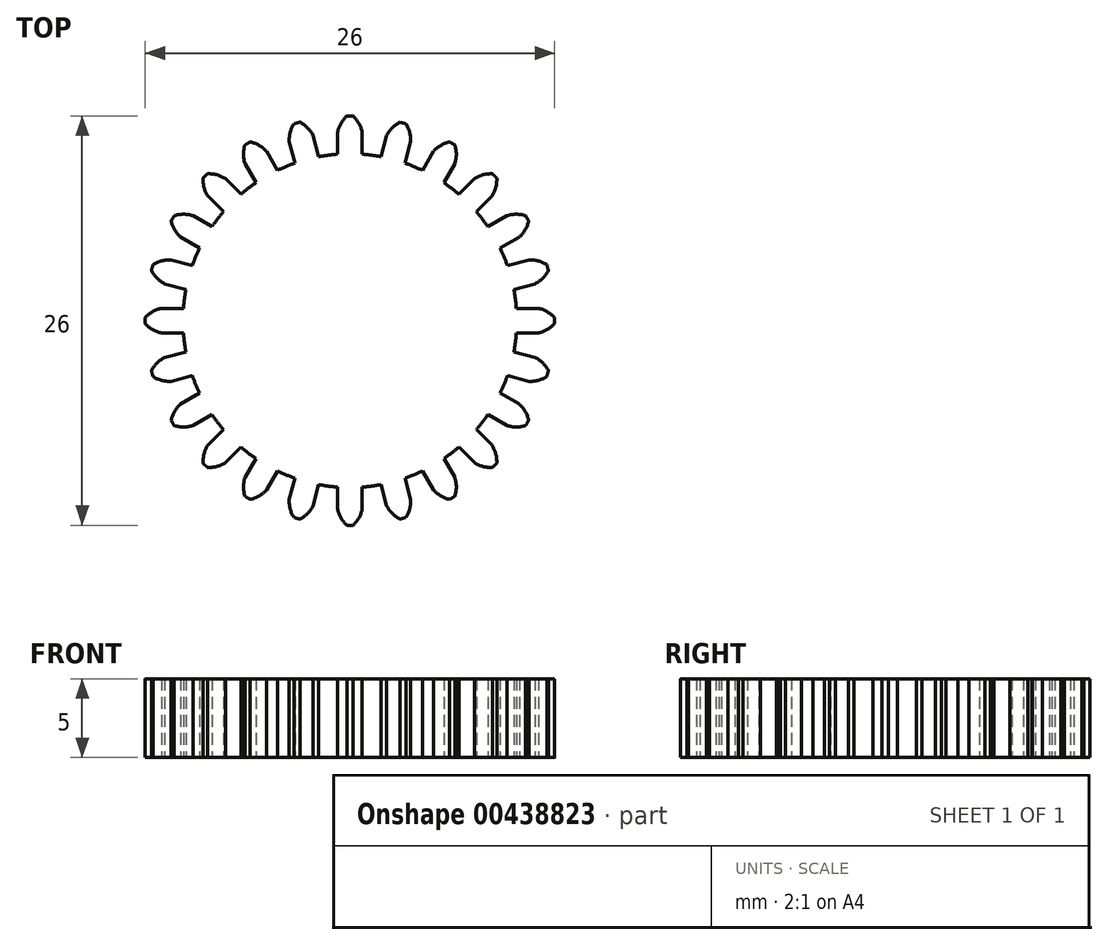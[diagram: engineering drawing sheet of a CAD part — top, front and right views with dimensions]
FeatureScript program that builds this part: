
annotation { "Feature Type Name" : "Feature", "Feature Type Description" : "" }
export const myFeature = defineFeature(function(context is Context, id is Id, definition is map)
    precondition{}
    {
        {
            var Q0;
            Q0=qCreatedBy(makeId("Top.planeOp"),FACE);
            var sketch = newSketch(context, id + "F0", { "sketchPlane" : qUnion([Q0])});
            skArc(sketch, "E0", {"start": v(-0.79, 12.98) * mm, "mid": v(0, -13) * mm, "end": v(0.79, 12.98) * mm, "construction": true});
            skCircle(sketch, "E1", {"center": v(0, 0) * mm, "radius": 12 * mm, "construction": true});
            skCircle(sketch, "E2", {"center": v(0, 0) * mm, "radius": 10.6 * mm, "construction": true});
            skLineSegment(sketch, "E3", {"start": v(-0.79, 10.57) * mm, "end": v(-0.79, 11.97) * mm});
            skLineSegment(sketch, "E4", {"start": v(0.79, 10.57) * mm, "end": v(0.79, 12.98) * mm});
            skArc(sketch, "E5", {"start": v(-0.2, 13) * mm, "mid": v(0, 13) * mm, "end": v(0.2, 13) * mm});
            skPoint(sketch, "E6.center", {"position": v(0.46, 5.44) * mm});
            skArc(sketch, "E7", {"start": v(0.79, 10.57) * mm, "mid": v(2.01, 10.4) * mm, "end": v(3.21, 10.1) * mm});
            skArc(sketch, "E8.1.0", {"start": v(-1.98, 10.41) * mm, "mid": v(-0.75, 10.57) * mm, "end": v(0.5, 10.59) * mm});
            skArc(sketch, "E8.2.0", {"start": v(-4.6, 9.55) * mm, "mid": v(-3.46, 10.02) * mm, "end": v(-2.27, 10.35) * mm});
            skArc(sketch, "E8.3.0", {"start": v(-6.92, 8.03) * mm, "mid": v(-5.94, 8.78) * mm, "end": v(-4.87, 9.42) * mm});
            skArc(sketch, "E8.4.0", {"start": v(-8.76, 5.97) * mm, "mid": v(-8, 6.95) * mm, "end": v(-7.14, 7.83) * mm});
            skArc(sketch, "E8.5.0", {"start": v(-10, 3.5) * mm, "mid": v(-9.53, 4.64) * mm, "end": v(-8.92, 5.72) * mm});
            skArc(sketch, "E8.6.0", {"start": v(-10.57, 0.79) * mm, "mid": v(-10.4, 2.01) * mm, "end": v(-10.1, 3.21) * mm});
            skArc(sketch, "E8.7.0", {"start": v(-10.41, -1.98) * mm, "mid": v(-10.57, -0.75) * mm, "end": v(-10.59, 0.5) * mm});
            skArc(sketch, "E8.8.0", {"start": v(-9.55, -4.6) * mm, "mid": v(-10.02, -3.46) * mm, "end": v(-10.35, -2.27) * mm});
            skArc(sketch, "E8.9.0", {"start": v(-8.03, -6.92) * mm, "mid": v(-8.78, -5.94) * mm, "end": v(-9.42, -4.87) * mm});
            skArc(sketch, "E8.10.0", {"start": v(-5.97, -8.76) * mm, "mid": v(-6.95, -8) * mm, "end": v(-7.83, -7.14) * mm});
            skArc(sketch, "E8.11.0", {"start": v(-3.5, -10) * mm, "mid": v(-4.64, -9.53) * mm, "end": v(-5.72, -8.92) * mm});
            skArc(sketch, "E8.12.0", {"start": v(-0.79, -10.57) * mm, "mid": v(-2.01, -10.4) * mm, "end": v(-3.21, -10.1) * mm});
            skArc(sketch, "E8.13.0", {"start": v(1.98, -10.41) * mm, "mid": v(0.75, -10.57) * mm, "end": v(-0.5, -10.59) * mm});
            skPoint(sketch, "E9", {"position": v(-0.79, 11.97) * mm});
            skPoint(sketch, "E10", {"position": v(0.79, 11.97) * mm});
            skPoint(sketch, "E11", {"position": v(0, 13) * mm});
            skPoint(sketch, "E11.positionSnap0", {"position": v(0, 13) * mm});
            skPoint(sketch, "E12", {"position": v(-0.2, 13) * mm});
            skArc(sketch, "E13", {"start": v(-0.2, 13) * mm, "mid": v(-0.57, 12.53) * mm, "end": v(-0.79, 11.97) * mm});
            skArc(sketch, "E14.MirrorCS", {"start": v(0.2, 13) * mm, "mid": v(0.57, 12.53) * mm, "end": v(0.79, 11.97) * mm});
            skArc(sketch, "E15.1.0", {"start": v(-3.55, 12.5) * mm, "mid": v(-3.8, 11.96) * mm, "end": v(-3.86, 11.36) * mm});
            skArc(sketch, "E15.1.1", {"start": v(-3.17, 12.6) * mm, "mid": v(-2.7, 12.25) * mm, "end": v(-2.34, 11.77) * mm});
            skArc(sketch, "E15.2.0", {"start": v(-6.67, 11.16) * mm, "mid": v(-6.76, 10.57) * mm, "end": v(-6.67, 9.98) * mm});
            skArc(sketch, "E15.2.1", {"start": v(-6.33, 11.35) * mm, "mid": v(-5.77, 11.14) * mm, "end": v(-5.3, 10.76) * mm});
            skArc(sketch, "E15.3.0", {"start": v(-9.33, 9.05) * mm, "mid": v(-9.26, 8.46) * mm, "end": v(-9.02, 7.91) * mm});
            skArc(sketch, "E15.3.1", {"start": v(-9.05, 9.33) * mm, "mid": v(-8.46, 9.26) * mm, "end": v(-7.91, 9.02) * mm});
            skArc(sketch, "E15.4.0", {"start": v(-11.35, 6.33) * mm, "mid": v(-11.14, 5.77) * mm, "end": v(-10.76, 5.3) * mm});
            skArc(sketch, "E15.4.1", {"start": v(-11.16, 6.67) * mm, "mid": v(-10.57, 6.76) * mm, "end": v(-9.98, 6.67) * mm});
            skArc(sketch, "E15.5.0", {"start": v(-12.6, 3.17) * mm, "mid": v(-12.25, 2.7) * mm, "end": v(-11.77, 2.34) * mm});
            skArc(sketch, "E15.5.1", {"start": v(-12.5, 3.55) * mm, "mid": v(-11.96, 3.8) * mm, "end": v(-11.36, 3.86) * mm});
            skArc(sketch, "E15.6.0", {"start": v(-13, -0.2) * mm, "mid": v(-12.53, -0.57) * mm, "end": v(-11.97, -0.79) * mm});
            skArc(sketch, "E15.6.1", {"start": v(-13, 0.2) * mm, "mid": v(-12.53, 0.57) * mm, "end": v(-11.97, 0.79) * mm});
            skArc(sketch, "E15.7.0", {"start": v(-12.5, -3.55) * mm, "mid": v(-11.96, -3.8) * mm, "end": v(-11.36, -3.86) * mm});
            skArc(sketch, "E15.7.1", {"start": v(-12.6, -3.17) * mm, "mid": v(-12.25, -2.7) * mm, "end": v(-11.77, -2.34) * mm});
            skArc(sketch, "E15.8.0", {"start": v(-11.16, -6.67) * mm, "mid": v(-10.57, -6.76) * mm, "end": v(-9.98, -6.67) * mm});
            skArc(sketch, "E15.8.1", {"start": v(-11.35, -6.33) * mm, "mid": v(-11.14, -5.77) * mm, "end": v(-10.76, -5.3) * mm});
            skArc(sketch, "E15.9.0", {"start": v(-9.05, -9.33) * mm, "mid": v(-8.46, -9.26) * mm, "end": v(-7.91, -9.02) * mm});
            skArc(sketch, "E15.9.1", {"start": v(-9.33, -9.05) * mm, "mid": v(-9.26, -8.46) * mm, "end": v(-9.02, -7.91) * mm});
            skArc(sketch, "E15.10.0", {"start": v(-6.33, -11.35) * mm, "mid": v(-5.77, -11.14) * mm, "end": v(-5.3, -10.76) * mm});
            skArc(sketch, "E15.10.1", {"start": v(-6.67, -11.16) * mm, "mid": v(-6.76, -10.57) * mm, "end": v(-6.67, -9.98) * mm});
            skArc(sketch, "E15.11.0", {"start": v(-3.17, -12.6) * mm, "mid": v(-2.7, -12.25) * mm, "end": v(-2.34, -11.77) * mm});
            skArc(sketch, "E15.11.1", {"start": v(-3.55, -12.5) * mm, "mid": v(-3.8, -11.96) * mm, "end": v(-3.86, -11.36) * mm});
            skArc(sketch, "E15.12.0", {"start": v(0.2, -13) * mm, "mid": v(0.57, -12.53) * mm, "end": v(0.79, -11.97) * mm});
            skArc(sketch, "E15.12.1", {"start": v(-0.2, -13) * mm, "mid": v(-0.57, -12.53) * mm, "end": v(-0.79, -11.97) * mm});
            skArc(sketch, "E15.13.0", {"start": v(3.55, -12.5) * mm, "mid": v(3.8, -11.96) * mm, "end": v(3.86, -11.36) * mm});
            skArc(sketch, "E15.13.1", {"start": v(3.17, -12.6) * mm, "mid": v(2.7, -12.25) * mm, "end": v(2.34, -11.77) * mm});
            skPoint(sketch, "E16.orphan", {"position": v(0.79, 12.98) * mm});
            skLineSegment(sketch, "E17", {"start": v(-0.79, 11.97) * mm, "end": v(-0.79, 12.98) * mm, "construction": true});
            skLineSegment(sketch, "E18.1.0", {"start": v(-3.5, 10) * mm, "end": v(-3.86, 11.36) * mm});
            skLineSegment(sketch, "E18.1.1", {"start": v(-1.98, 10.41) * mm, "end": v(-2.6, 12.74) * mm});
            skLineSegment(sketch, "E18.2.0", {"start": v(-5.97, 8.76) * mm, "end": v(-6.67, 9.98) * mm});
            skLineSegment(sketch, "E18.2.1", {"start": v(-4.6, 9.55) * mm, "end": v(-5.8, 11.63) * mm});
            skLineSegment(sketch, "E18.3.0", {"start": v(-8.03, 6.92) * mm, "end": v(-9.02, 7.91) * mm});
            skLineSegment(sketch, "E18.3.1", {"start": v(-6.92, 8.03) * mm, "end": v(-8.62, 9.73) * mm});
            skLineSegment(sketch, "E18.4.0", {"start": v(-9.55, 4.6) * mm, "end": v(-10.76, 5.3) * mm});
            skLineSegment(sketch, "E18.4.1", {"start": v(-8.76, 5.97) * mm, "end": v(-10.85, 7.17) * mm});
            skLineSegment(sketch, "E18.5.0", {"start": v(-10.41, 1.98) * mm, "end": v(-11.77, 2.34) * mm});
            skLineSegment(sketch, "E18.5.1", {"start": v(-10, 3.5) * mm, "end": v(-12.33, 4.12) * mm});
            skLineSegment(sketch, "E18.6.0", {"start": v(-10.57, -0.79) * mm, "end": v(-11.97, -0.79) * mm});
            skLineSegment(sketch, "E18.6.1", {"start": v(-10.57, 0.79) * mm, "end": v(-12.98, 0.79) * mm});
            skLineSegment(sketch, "E18.7.0", {"start": v(-10, -3.5) * mm, "end": v(-11.36, -3.86) * mm});
            skLineSegment(sketch, "E18.7.1", {"start": v(-10.41, -1.98) * mm, "end": v(-12.74, -2.6) * mm});
            skLineSegment(sketch, "E18.8.0", {"start": v(-8.76, -5.97) * mm, "end": v(-9.98, -6.67) * mm});
            skLineSegment(sketch, "E18.8.1", {"start": v(-9.55, -4.6) * mm, "end": v(-11.63, -5.8) * mm});
            skLineSegment(sketch, "E18.9.0", {"start": v(-6.92, -8.03) * mm, "end": v(-7.91, -9.02) * mm});
            skLineSegment(sketch, "E18.9.1", {"start": v(-8.03, -6.92) * mm, "end": v(-9.73, -8.62) * mm});
            skLineSegment(sketch, "E18.10.0", {"start": v(-4.6, -9.55) * mm, "end": v(-5.3, -10.76) * mm});
            skLineSegment(sketch, "E18.10.1", {"start": v(-5.97, -8.76) * mm, "end": v(-7.17, -10.85) * mm});
            skLineSegment(sketch, "E18.11.0", {"start": v(-1.98, -10.41) * mm, "end": v(-2.34, -11.77) * mm});
            skLineSegment(sketch, "E18.11.1", {"start": v(-3.5, -10) * mm, "end": v(-4.12, -12.33) * mm});
            skLineSegment(sketch, "E18.12.0", {"start": v(0.79, -10.57) * mm, "end": v(0.79, -11.97) * mm});
            skLineSegment(sketch, "E18.12.1", {"start": v(-0.79, -10.57) * mm, "end": v(-0.79, -12.98) * mm});
            skLineSegment(sketch, "E18.13.0", {"start": v(3.5, -10) * mm, "end": v(3.86, -11.36) * mm});
            skLineSegment(sketch, "E18.13.1", {"start": v(1.98, -10.41) * mm, "end": v(2.6, -12.74) * mm});
            skArc(sketch, "E19.1.0", {"start": v(-3.55, 12.5) * mm, "mid": v(-3.36, 12.56) * mm, "end": v(-3.17, 12.6) * mm});
            skArc(sketch, "E19.2.0", {"start": v(-6.67, 11.16) * mm, "mid": v(-6.5, 11.26) * mm, "end": v(-6.33, 11.35) * mm});
            skArc(sketch, "E19.3.0", {"start": v(-9.33, 9.05) * mm, "mid": v(-9.2, 9.2) * mm, "end": v(-9.05, 9.33) * mm});
            skArc(sketch, "E19.4.0", {"start": v(-11.35, 6.33) * mm, "mid": v(-11.26, 6.5) * mm, "end": v(-11.16, 6.67) * mm});
            skArc(sketch, "E19.5.0", {"start": v(-12.6, 3.17) * mm, "mid": v(-12.56, 3.36) * mm, "end": v(-12.5, 3.55) * mm});
            skArc(sketch, "E19.6.0", {"start": v(-13, -0.2) * mm, "mid": v(-13, 0) * mm, "end": v(-13, 0.2) * mm});
            skArc(sketch, "E19.7.0", {"start": v(-12.5, -3.55) * mm, "mid": v(-12.56, -3.36) * mm, "end": v(-12.6, -3.17) * mm});
            skArc(sketch, "E19.8.0", {"start": v(-11.16, -6.67) * mm, "mid": v(-11.26, -6.5) * mm, "end": v(-11.35, -6.33) * mm});
            skArc(sketch, "E19.9.0", {"start": v(-9.05, -9.33) * mm, "mid": v(-9.2, -9.2) * mm, "end": v(-9.33, -9.05) * mm});
            skArc(sketch, "E19.10.0", {"start": v(-6.33, -11.35) * mm, "mid": v(-6.5, -11.26) * mm, "end": v(-6.67, -11.16) * mm});
            skArc(sketch, "E19.11.0", {"start": v(-3.17, -12.6) * mm, "mid": v(-3.36, -12.56) * mm, "end": v(-3.55, -12.5) * mm});
            skArc(sketch, "E19.12.0", {"start": v(0.2, -13) * mm, "mid": v(0, -13) * mm, "end": v(-0.2, -13) * mm});
            skArc(sketch, "E19.13.0", {"start": v(3.55, -12.5) * mm, "mid": v(3.36, -12.56) * mm, "end": v(3.17, -12.6) * mm});
            skArc(sketch, "E20.3.14.0", {"start": v(6.67, -11.16) * mm, "mid": v(6.76, -10.57) * mm, "end": v(6.67, -9.98) * mm});
            skArc(sketch, "E20.4.14.0", {"start": v(6.33, -11.35) * mm, "mid": v(5.77, -11.14) * mm, "end": v(5.3, -10.76) * mm});
            skArc(sketch, "E20.3.15.0", {"start": v(9.33, -9.05) * mm, "mid": v(9.26, -8.46) * mm, "end": v(9.02, -7.91) * mm});
            skArc(sketch, "E20.4.15.0", {"start": v(9.05, -9.33) * mm, "mid": v(8.46, -9.26) * mm, "end": v(7.91, -9.02) * mm});
            skArc(sketch, "E20.3.16.0", {"start": v(11.35, -6.33) * mm, "mid": v(11.14, -5.77) * mm, "end": v(10.76, -5.3) * mm});
            skArc(sketch, "E20.4.16.0", {"start": v(11.16, -6.67) * mm, "mid": v(10.57, -6.76) * mm, "end": v(9.98, -6.67) * mm});
            skArc(sketch, "E20.3.17.0", {"start": v(12.6, -3.17) * mm, "mid": v(12.25, -2.7) * mm, "end": v(11.77, -2.34) * mm});
            skArc(sketch, "E20.4.17.0", {"start": v(12.5, -3.55) * mm, "mid": v(11.96, -3.8) * mm, "end": v(11.36, -3.86) * mm});
            skArc(sketch, "E20.3.18.0", {"start": v(13, 0.2) * mm, "mid": v(12.53, 0.57) * mm, "end": v(11.97, 0.79) * mm});
            skArc(sketch, "E20.4.18.0", {"start": v(13, -0.2) * mm, "mid": v(12.53, -0.57) * mm, "end": v(11.97, -0.79) * mm});
            skArc(sketch, "E20.3.19.0", {"start": v(12.5, 3.55) * mm, "mid": v(11.96, 3.8) * mm, "end": v(11.36, 3.86) * mm});
            skArc(sketch, "E20.4.19.0", {"start": v(12.6, 3.17) * mm, "mid": v(12.25, 2.7) * mm, "end": v(11.77, 2.34) * mm});
            skArc(sketch, "E20.3.20.0", {"start": v(11.16, 6.67) * mm, "mid": v(10.57, 6.76) * mm, "end": v(9.98, 6.67) * mm});
            skArc(sketch, "E20.4.20.0", {"start": v(11.35, 6.33) * mm, "mid": v(11.14, 5.77) * mm, "end": v(10.76, 5.3) * mm});
            skArc(sketch, "E20.3.21.0", {"start": v(9.05, 9.33) * mm, "mid": v(8.46, 9.26) * mm, "end": v(7.91, 9.02) * mm});
            skArc(sketch, "E20.4.21.0", {"start": v(9.33, 9.05) * mm, "mid": v(9.26, 8.46) * mm, "end": v(9.02, 7.91) * mm});
            skArc(sketch, "E20.3.22.0", {"start": v(6.33, 11.35) * mm, "mid": v(5.77, 11.14) * mm, "end": v(5.3, 10.76) * mm});
            skArc(sketch, "E20.4.22.0", {"start": v(6.67, 11.16) * mm, "mid": v(6.76, 10.57) * mm, "end": v(6.67, 9.98) * mm});
            skArc(sketch, "E20.3.23.0", {"start": v(3.17, 12.6) * mm, "mid": v(2.7, 12.25) * mm, "end": v(2.34, 11.77) * mm});
            skArc(sketch, "E20.4.23.0", {"start": v(3.55, 12.5) * mm, "mid": v(3.8, 11.96) * mm, "end": v(3.86, 11.36) * mm});
            skArc(sketch, "E21.2.14.0", {"start": v(4.6, -9.55) * mm, "mid": v(3.46, -10.02) * mm, "end": v(2.27, -10.35) * mm});
            skArc(sketch, "E21.2.15.0", {"start": v(6.92, -8.03) * mm, "mid": v(5.94, -8.78) * mm, "end": v(4.87, -9.42) * mm});
            skArc(sketch, "E21.2.16.0", {"start": v(8.76, -5.97) * mm, "mid": v(8, -6.95) * mm, "end": v(7.14, -7.83) * mm});
            skArc(sketch, "E21.2.17.0", {"start": v(10, -3.5) * mm, "mid": v(9.53, -4.64) * mm, "end": v(8.92, -5.72) * mm});
            skArc(sketch, "E21.2.18.0", {"start": v(10.57, -0.79) * mm, "mid": v(10.4, -2.01) * mm, "end": v(10.1, -3.21) * mm});
            skArc(sketch, "E21.2.19.0", {"start": v(10.41, 1.98) * mm, "mid": v(10.57, 0.75) * mm, "end": v(10.59, -0.5) * mm});
            skArc(sketch, "E21.2.20.0", {"start": v(9.55, 4.6) * mm, "mid": v(10.02, 3.46) * mm, "end": v(10.35, 2.27) * mm});
            skArc(sketch, "E21.2.21.0", {"start": v(8.03, 6.92) * mm, "mid": v(8.78, 5.94) * mm, "end": v(9.42, 4.87) * mm});
            skArc(sketch, "E21.2.22.0", {"start": v(5.97, 8.76) * mm, "mid": v(6.95, 8) * mm, "end": v(7.83, 7.14) * mm});
            skArc(sketch, "E21.2.23.0", {"start": v(3.5, 10) * mm, "mid": v(4.64, 9.53) * mm, "end": v(5.72, 8.92) * mm});
            skLineSegment(sketch, "E22.1.14.0", {"start": v(5.97, -8.76) * mm, "end": v(6.67, -9.98) * mm});
            skLineSegment(sketch, "E22.3.14.0", {"start": v(4.6, -9.55) * mm, "end": v(5.8, -11.63) * mm});
            skLineSegment(sketch, "E22.1.15.0", {"start": v(8.03, -6.92) * mm, "end": v(9.02, -7.91) * mm});
            skLineSegment(sketch, "E22.3.15.0", {"start": v(6.92, -8.03) * mm, "end": v(8.62, -9.73) * mm});
            skLineSegment(sketch, "E22.1.16.0", {"start": v(9.55, -4.6) * mm, "end": v(10.76, -5.3) * mm});
            skLineSegment(sketch, "E22.3.16.0", {"start": v(8.76, -5.97) * mm, "end": v(10.85, -7.17) * mm});
            skLineSegment(sketch, "E22.1.17.0", {"start": v(10.41, -1.98) * mm, "end": v(11.77, -2.34) * mm});
            skLineSegment(sketch, "E22.3.17.0", {"start": v(10, -3.5) * mm, "end": v(12.33, -4.12) * mm});
            skLineSegment(sketch, "E22.1.18.0", {"start": v(10.57, 0.79) * mm, "end": v(11.97, 0.79) * mm});
            skLineSegment(sketch, "E22.3.18.0", {"start": v(10.57, -0.79) * mm, "end": v(12.98, -0.79) * mm});
            skLineSegment(sketch, "E22.1.19.0", {"start": v(10, 3.5) * mm, "end": v(11.36, 3.86) * mm});
            skLineSegment(sketch, "E22.3.19.0", {"start": v(10.41, 1.98) * mm, "end": v(12.74, 2.6) * mm});
            skLineSegment(sketch, "E22.1.20.0", {"start": v(8.76, 5.97) * mm, "end": v(9.98, 6.67) * mm});
            skLineSegment(sketch, "E22.3.20.0", {"start": v(9.55, 4.6) * mm, "end": v(11.63, 5.8) * mm});
            skLineSegment(sketch, "E22.1.21.0", {"start": v(6.92, 8.03) * mm, "end": v(7.91, 9.02) * mm});
            skLineSegment(sketch, "E22.3.21.0", {"start": v(8.03, 6.92) * mm, "end": v(9.73, 8.62) * mm});
            skLineSegment(sketch, "E22.1.22.0", {"start": v(4.6, 9.55) * mm, "end": v(5.3, 10.76) * mm});
            skLineSegment(sketch, "E22.3.22.0", {"start": v(5.97, 8.76) * mm, "end": v(7.17, 10.85) * mm});
            skLineSegment(sketch, "E22.1.23.0", {"start": v(1.98, 10.41) * mm, "end": v(2.34, 11.77) * mm});
            skLineSegment(sketch, "E22.3.23.0", {"start": v(3.5, 10) * mm, "end": v(4.12, 12.33) * mm});
            skArc(sketch, "E23.1.14.0", {"start": v(6.67, -11.16) * mm, "mid": v(6.5, -11.26) * mm, "end": v(6.33, -11.35) * mm});
            skArc(sketch, "E23.1.15.0", {"start": v(9.33, -9.05) * mm, "mid": v(9.2, -9.2) * mm, "end": v(9.05, -9.33) * mm});
            skArc(sketch, "E23.1.16.0", {"start": v(11.35, -6.33) * mm, "mid": v(11.26, -6.5) * mm, "end": v(11.16, -6.67) * mm});
            skArc(sketch, "E23.1.17.0", {"start": v(12.6, -3.17) * mm, "mid": v(12.56, -3.36) * mm, "end": v(12.5, -3.55) * mm});
            skArc(sketch, "E23.1.18.0", {"start": v(13, 0.2) * mm, "mid": v(13, 0) * mm, "end": v(13, -0.2) * mm});
            skArc(sketch, "E23.1.19.0", {"start": v(12.5, 3.55) * mm, "mid": v(12.56, 3.36) * mm, "end": v(12.6, 3.17) * mm});
            skArc(sketch, "E23.1.20.0", {"start": v(11.16, 6.67) * mm, "mid": v(11.26, 6.5) * mm, "end": v(11.35, 6.33) * mm});
            skArc(sketch, "E23.1.21.0", {"start": v(9.05, 9.33) * mm, "mid": v(9.2, 9.2) * mm, "end": v(9.33, 9.05) * mm});
            skArc(sketch, "E23.1.22.0", {"start": v(6.33, 11.35) * mm, "mid": v(6.5, 11.26) * mm, "end": v(6.67, 11.16) * mm});
            skArc(sketch, "E23.1.23.0", {"start": v(3.17, 12.6) * mm, "mid": v(3.36, 12.56) * mm, "end": v(3.55, 12.5) * mm});
            skSolve(sketch);
        }
        {
            var Q0;
            Q0 = qSketchRegion(id + "F0", true);
            extrude(context, id + "F1", {"entities" : qUnion([Q0]), "depth" : 5 * mm});
        }
    });
